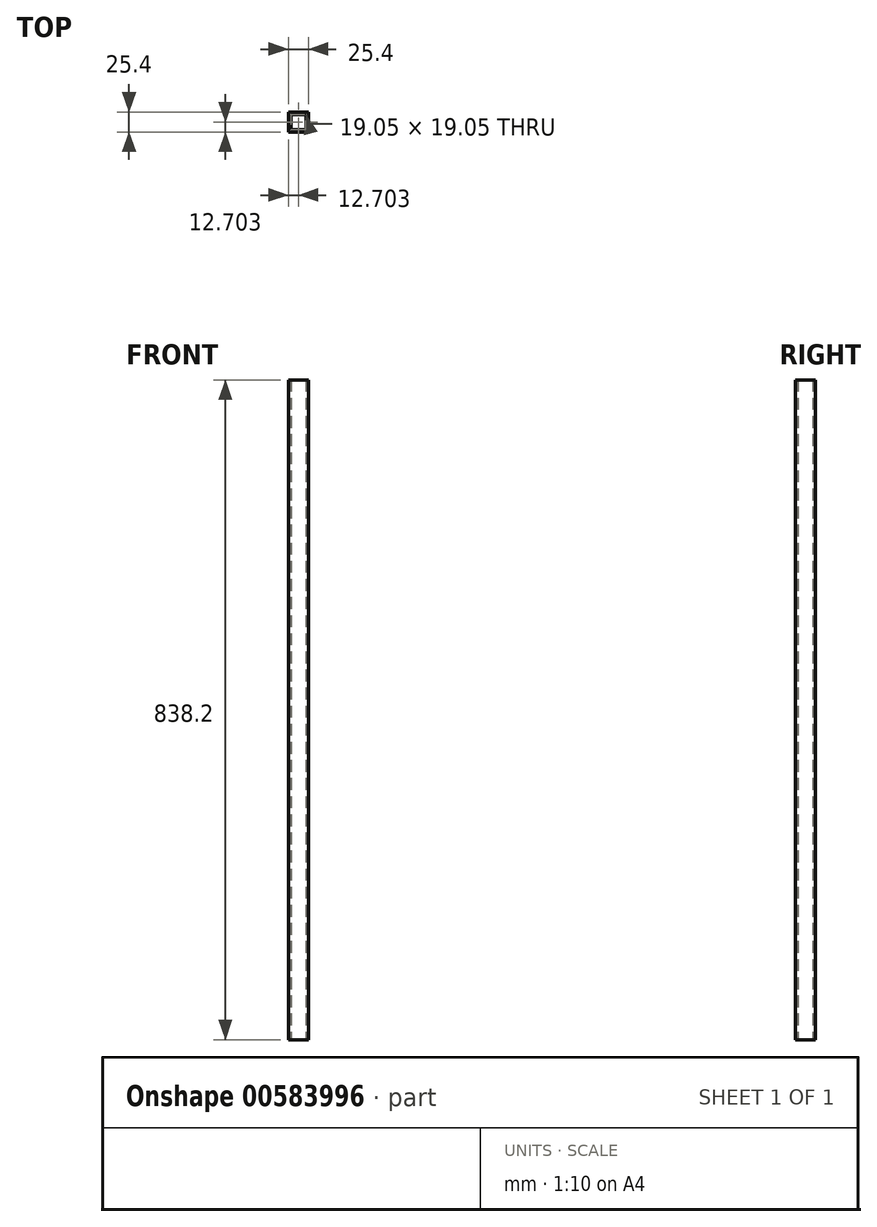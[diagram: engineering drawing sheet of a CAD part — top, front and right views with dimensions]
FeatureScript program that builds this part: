
annotation { "Feature Type Name" : "Feature", "Feature Type Description" : "" }
export const myFeature = defineFeature(function(context is Context, id is Id, definition is map)
    precondition{}
    {
        {
            var Q0;
            Q0=qCreatedBy(makeId("Top.planeOp"),FACE);
            var sketch = newSketch(context, id + "F0", { "sketchPlane" : qUnion([Q0])});
            skLineSegment(sketch, "E0.bottom", {"start": v(-6.57, 8.24) * mm, "end": v(12.48, 8.24) * mm});
            skLineSegment(sketch, "E0.top", {"start": v(-6.57, -10.81) * mm, "end": v(12.48, -10.81) * mm});
            skLineSegment(sketch, "E0.left", {"start": v(-6.57, 8.24) * mm, "end": v(-6.57, -10.81) * mm});
            skLineSegment(sketch, "E0.right", {"start": v(12.48, 8.24) * mm, "end": v(12.48, -10.81) * mm});
            skLineSegment(sketch, "E1.bottom", {"start": v(-9.75, 11.41) * mm, "end": v(15.65, 11.41) * mm});
            skLineSegment(sketch, "E1.top", {"start": v(-9.75, -13.99) * mm, "end": v(15.65, -13.99) * mm});
            skLineSegment(sketch, "E1.left", {"start": v(-9.75, 11.41) * mm, "end": v(-9.75, -13.99) * mm});
            skLineSegment(sketch, "E1.right", {"start": v(15.65, 11.41) * mm, "end": v(15.65, -13.99) * mm});
            skSolve(sketch);
        }
        {
            var Q0;
            Q0=makeQuery(id+"F0.imprint","IMPRINT",FACE,{"disambiguationData":[TD([[makeQuery(id+"F0.imprint","IMPRINT",EDGE,{"derivedFrom":sQuery(id+"F0.wireOp",EDGE,"E0.bottom")}),1.0]])]});
            extrude(context, id + "F1", {"entities" : qUnion([Q0]), "depth" : 838.2 * mm, "offsetDistance" : 25.4 * mm});
        }
    });
